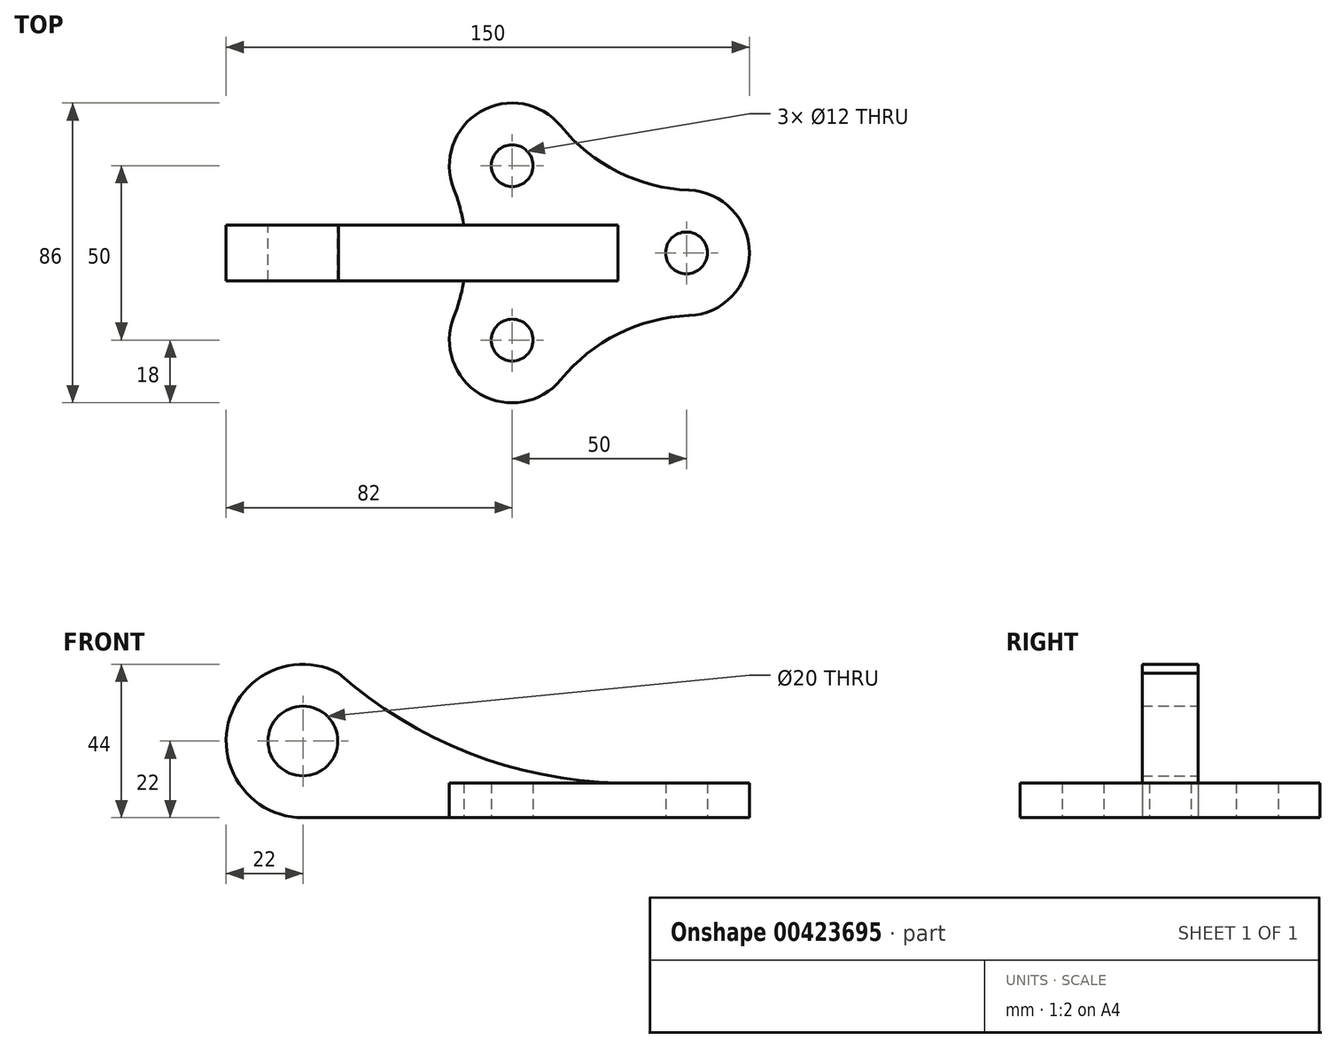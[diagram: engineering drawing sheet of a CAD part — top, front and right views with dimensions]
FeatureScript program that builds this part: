
annotation { "Feature Type Name" : "Feature", "Feature Type Description" : "" }
export const myFeature = defineFeature(function(context is Context, id is Id, definition is map)
    precondition{}
    {
        {
            var Q0;
            Q0=qCreatedBy(makeId("Top.planeOp"),FACE);
            var sketch = newSketch(context, id + "F0", { "sketchPlane" : qUnion([Q0])});
            skCircle(sketch, "E0", {"center": v(0, 0) * mm, "radius": 6 * mm});
            skCircle(sketch, "E1", {"center": v(-50, 25) * mm, "radius": 6 * mm});
            skCircle(sketch, "E2", {"center": v(-50, -25) * mm, "radius": 6 * mm});
            skArc(sketch, "E3", {"start": v(0.72, -17.99) * mm, "mid": v(18, 0) * mm, "end": v(0.72, 17.99) * mm});
            skArc(sketch, "E4", {"start": v(-36.04, 36.37) * mm, "mid": v(-59.1, 40.53) * mm, "end": v(-66.74, 18.38) * mm});
            skArc(sketch, "E5", {"start": v(-66.74, -18.38) * mm, "mid": v(-59.1, -40.53) * mm, "end": v(-36.04, -36.37) * mm});
            skArc(sketch, "E6", {"start": v(-36.04, 36.37) * mm, "mid": v(-19.64, 23.22) * mm, "end": v(0.72, 17.99) * mm});
            skArc(sketch, "E7", {"start": v(-66.74, -18.38) * mm, "mid": v(-63.24, 0) * mm, "end": v(-66.74, 18.38) * mm});
            skArc(sketch, "E8", {"start": v(0.72, -17.99) * mm, "mid": v(-19.64, -23.22) * mm, "end": v(-36.04, -36.37) * mm});
            skSolve(sketch);
        }
        {
            var Q0;
            Q0 = qSketchRegion(id + "F0", true);
            extrude(context, id + "F1", {"entities" : qUnion([Q0]), "depth" : 10 * mm});
        }
        {
            var Q0;
            Q0=qCreatedBy(makeId("Front.planeOp"),FACE);
            var sketch = newSketch(context, id + "F2", { "sketchPlane" : qUnion([Q0])});
            skCircle(sketch, "E9", {"center": v(-110, 22) * mm, "radius": 10 * mm});
            skArc(sketch, "E10", {"start": v(-99.77, 41.48) * mm, "mid": v(-131.36, 27.27) * mm, "end": v(-110, 0) * mm});
            skLineSegment(sketch, "E11", {"start": v(-13.99, 0) * mm, "end": v(-110, 0) * mm});
            skLineSegment(sketch, "E12.0", {"start": v(0.72, 10) * mm, "end": v(-36.04, 10) * mm});
            skArc(sketch, "E13", {"start": v(-99.77, 41.48) * mm, "mid": v(-59.86, 17.62) * mm, "end": v(-13.99, 10) * mm});
            skLineSegment(sketch, "E14", {"start": v(-13.99, 10) * mm, "end": v(-13.99, 0) * mm});
            skSolve(sketch);
        }
        {
            var Q0;
            Q0 = qSketchRegion(id + "F2", true);
            extrude(context, id + "F3", {"entities" : qUnion([Q0]), "operationType" : NewBodyOperationType.ADD, "endBound" : BoundingType.SYMMETRIC, "depth" : 16 * mm});
        }
    });
